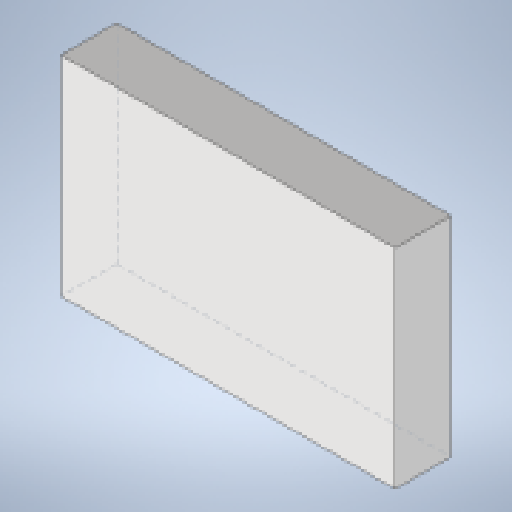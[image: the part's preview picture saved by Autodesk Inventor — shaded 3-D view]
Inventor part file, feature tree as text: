
AUTODESK INVENTOR PART (.ipt)
format: ipt  version: 2024 (Build 280153000, 153)  size: 176,640 bytes
history: native  units: in
note: dims shown in document units (in); Inventor stores cm internally (conversion verified against a paired STEP export)
features: extrude x1, fillet x1, sketch x1
ambient origin geometry x8: Origin, YZ Plane, XZ Plane, XY Plane, X Axis, Y Axis, Z Axis, Center Point
bodies: Solid1 (feature_tree)
feature tree (3):
  extrude  "Extrusion1"  Depth=1.8898in
  fillet  "Fillet1"  Radius=0.315in
  sketch  "Sketch1"  dims[d3=1.1811in d4=1.8898in d7=0.315in d8=0.0in d9=0.0787in]
